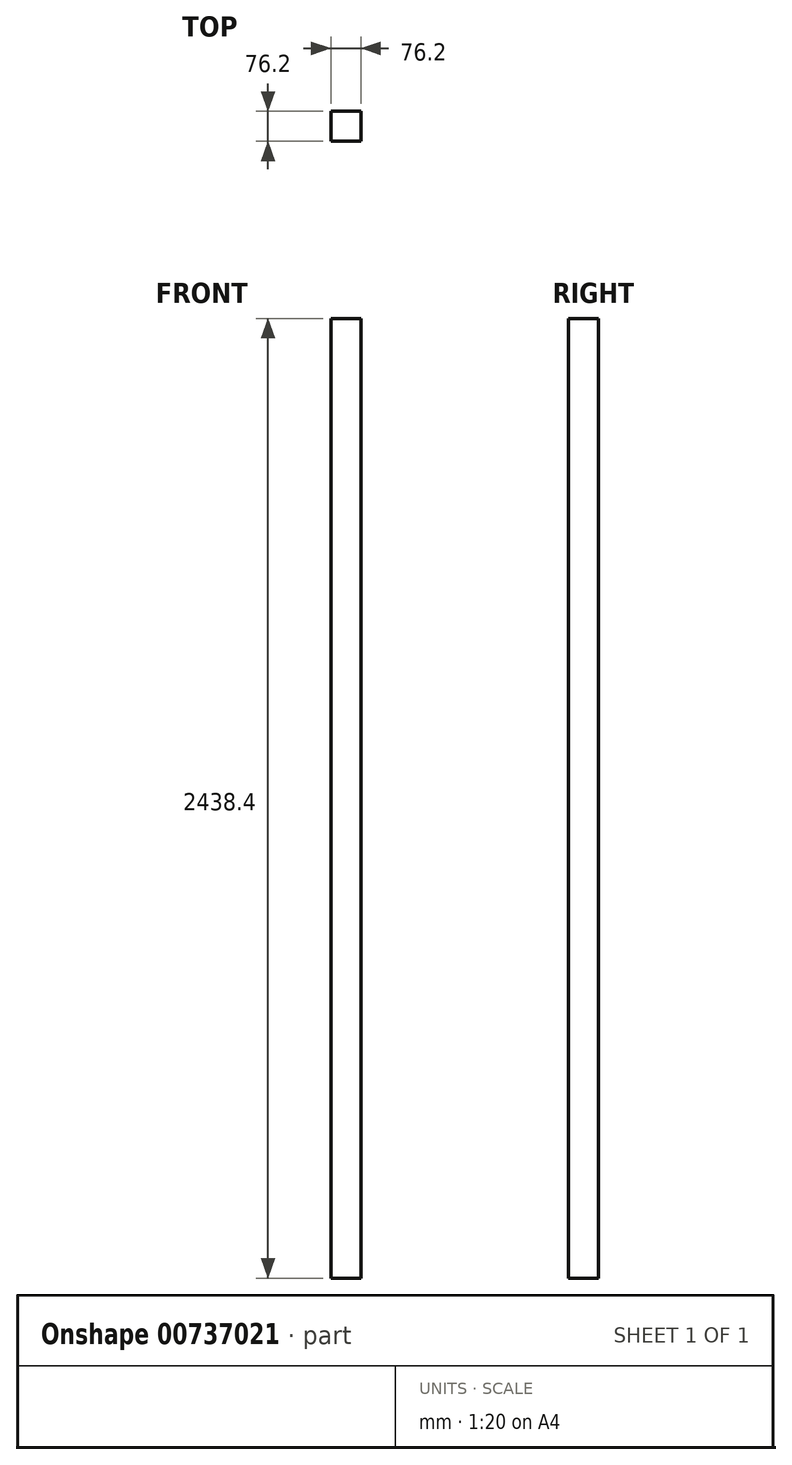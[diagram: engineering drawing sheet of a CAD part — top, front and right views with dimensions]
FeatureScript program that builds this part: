
annotation { "Feature Type Name" : "Feature", "Feature Type Description" : "" }
export const myFeature = defineFeature(function(context is Context, id is Id, definition is map)
    precondition{}
    {
        {
            var Q0;
            Q0=qCreatedBy(makeId("Top.planeOp"),FACE);
            var sketch = newSketch(context, id + "F0", { "sketchPlane" : qUnion([Q0])});
            skLineSegment(sketch, "E0.bottom", {"start": v(-34.27, 42.21) * mm, "end": v(41.93, 42.21) * mm});
            skLineSegment(sketch, "E0.top", {"start": v(-34.27, -33.99) * mm, "end": v(41.93, -33.99) * mm});
            skLineSegment(sketch, "E0.left", {"start": v(-34.27, 42.21) * mm, "end": v(-34.27, -33.99) * mm});
            skLineSegment(sketch, "E0.right", {"start": v(41.93, 42.21) * mm, "end": v(41.93, -33.99) * mm});
            skSolve(sketch);
        }
        {
            var Q0;
            Q0=makeQuery(id+"F0.imprint","IMPRINT",FACE,{"disambiguationData":[TD([[makeQuery(id+"F0.imprint","IMPRINT",EDGE,{"derivedFrom":sQuery(id+"F0.wireOp",EDGE,"E0.bottom")}),-1.0]])]});
            extrude(context, id + "F1", {"entities" : qUnion([Q0]), "depth" : 2438.4 * mm, "offsetDistance" : 25.4 * mm});
        }
    });
